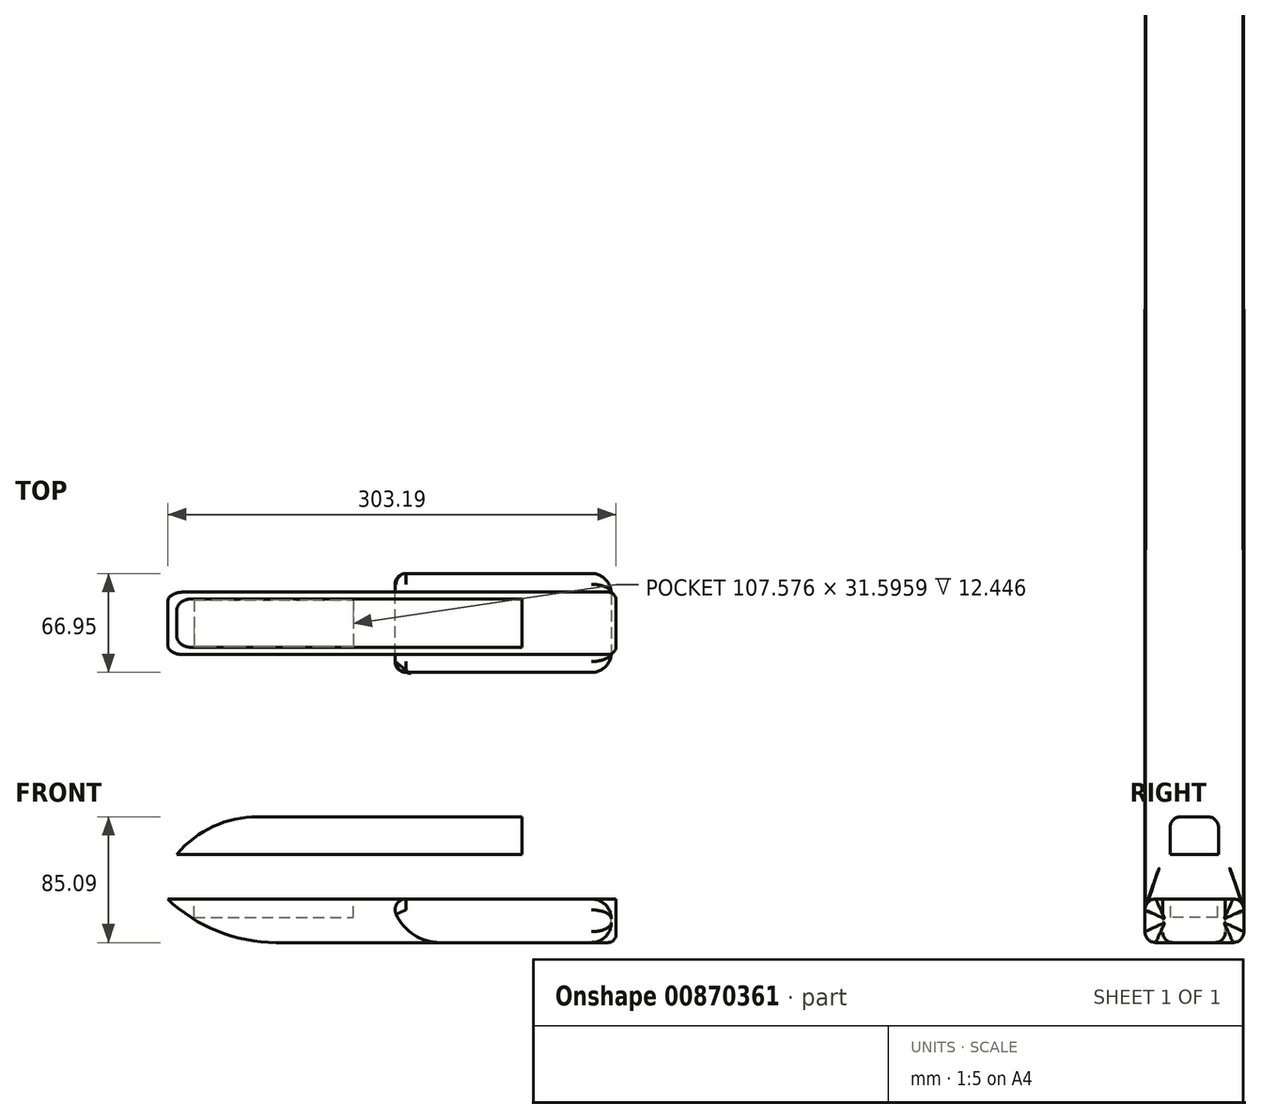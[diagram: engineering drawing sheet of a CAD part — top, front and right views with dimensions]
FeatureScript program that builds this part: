
annotation { "Feature Type Name" : "Feature", "Feature Type Description" : "" }
export const myFeature = defineFeature(function(context is Context, id is Id, definition is map)
    precondition{}
    {
        {
            var Q0;
            Q0=qCreatedBy(makeId("Top.planeOp"),FACE);
            var sketch = newSketch(context, id + "F0", { "sketchPlane" : qUnion([Q0])});
            skLineSegment(sketch, "E0.bottom", {"start": v(-65.35, -62.71) * mm, "end": v(74.53, -62.71) * mm});
            skLineSegment(sketch, "E0.top", {"start": v(-65.35, -29.97) * mm, "end": v(74.53, -29.97) * mm});
            skLineSegment(sketch, "E0.left", {"start": v(-65.35, -62.71) * mm, "end": v(-65.35, -29.97) * mm});
            skLineSegment(sketch, "E0.right", {"start": v(74.53, -62.71) * mm, "end": v(74.53, -29.97) * mm});
            skSolve(sketch);
        }
        {
            var Q0;
            Q0 = qSketchRegion(id + "F0", true);
            var Q1;
            Q1=makeQuery(id+"F0.imprint","IMPRINT",FACE,{"disambiguationData":[TD([[makeQuery(id+"F0.imprint","IMPRINT",EDGE,{"derivedFrom":sQuery(id+"F0.wireOp",EDGE,"E0.bottom")}),1.0]])]});
            extrude(context, id + "F1", {"entities" : qUnion([Q0, Q1]), "depth" : 25.4 * mm, "offsetDistance" : 25.4 * mm});
        }
        {
            var Q0;
            Q0=makeQuery(id+"F1.opExtrude","CAP_EDGE",EDGE,{"disambiguationData":[OSD([sQuery(id+"F0.wireOp",EDGE,"E0.left")])],"isStart":false});
            fillet(context, id + "F2", {"entities" : qUnion([Q0]), "radius" : 71.75 * mm, "tangentPropagation" : true, "allowEdgeOverflow" : false});
        }
        {
            var Q0;
            Q0=makeQuery(id+"F1.opExtrude","CAP_EDGE",EDGE,{"disambiguationData":[OSD([sQuery(id+"F0.wireOp",EDGE,"E0.bottom")])],"isStart":false});
            var Q1;
            Q1=makeQuery(id+"F1.opExtrude","CAP_EDGE",EDGE,{"disambiguationData":[OSD([sQuery(id+"F0.wireOp",EDGE,"E0.top")])],"isStart":false});
            fillet(context, id + "F3", {"entities" : qUnion([Q0, Q1]), "radius" : 7.36 * mm, "tangentPropagation" : true, "allowEdgeOverflow" : false});
        }
        {
            var Q0;
            Q0=makeQuery(id+"F1.opExtrude","SWEPT_FACE",FACE,{"disambiguationData":[OSD([sQuery(id+"F0.wireOp",EDGE,"E0.right")])]});
            extrude(context, id + "F4", {"entities" : qUnion([Q0]), "operationType" : NewBodyOperationType.ADD, "depth" : 93.22 * mm, "offsetDistance" : 25.4 * mm});
        }
        {
            var Q0;
            Q0=qCreatedBy(makeId("Top.planeOp"),FACE);
            cPlane(context, id + "F5", {"entities" : qUnion([Q0]), "cplaneType" : CPlaneType.OFFSET, "offset" : 30.23 * mm, "oppositeDirection" : true, "width" : 152.4 * mm, "height" : 152.4 * mm});
        }
        {
            var Q0;
            Q0=qCreatedBy(id+"F5.planeOp",FACE);
            var sketch = newSketch(context, id + "F6", { "sketchPlane" : qUnion([Q0])});
            skLineSegment(sketch, "E1.bottom", {"start": v(80.05, -12.74) * mm, "end": v(228.25, -12.74) * mm});
            skLineSegment(sketch, "E1.top", {"start": v(80.05, -79.7) * mm, "end": v(228.25, -79.7) * mm});
            skLineSegment(sketch, "E1.left", {"start": v(80.05, -12.74) * mm, "end": v(80.05, -79.7) * mm});
            skLineSegment(sketch, "E1.right", {"start": v(228.25, -12.74) * mm, "end": v(228.25, -79.7) * mm});
            skPoint(sketch, "E1.middle", {"position": v(154.15, -46.22) * mm});
            skSolve(sketch);
        }
        {
            var Q0;
            Q0=qCreatedBy(id+"F5.planeOp",FACE);
            var sketch = newSketch(context, id + "F7", { "sketchPlane" : qUnion([Q0])});
            skLineSegment(sketch, "E2.bottom", {"start": v(-71.65, -25.4) * mm, "end": v(231.54, -25.4) * mm});
            skLineSegment(sketch, "E2.top", {"start": v(-71.65, -67.57) * mm, "end": v(231.54, -67.57) * mm});
            skLineSegment(sketch, "E2.left", {"start": v(-71.65, -25.4) * mm, "end": v(-71.65, -67.57) * mm});
            skLineSegment(sketch, "E2.right", {"start": v(231.54, -25.4) * mm, "end": v(231.54, -67.57) * mm});
            skPoint(sketch, "E2.middle", {"position": v(79.94, -46.48) * mm});
            skSolve(sketch);
        }
        {
            var Q0;
            Q0=makeQuery(id+"F6.imprint","IMPRINT",FACE,{"disambiguationData":[TD([[makeQuery(id+"F6.imprint","IMPRINT",EDGE,{"derivedFrom":sQuery(id+"F6.wireOp",EDGE,"E1.bottom")}),-1.0]])]});
            var Q1;
            Q1=makeQuery(id+"F7.imprint","IMPRINT",FACE,{"disambiguationData":[TD([[makeQuery(id+"F7.imprint","IMPRINT",EDGE,{"derivedFrom":sQuery(id+"F7.wireOp",EDGE,"E2.bottom")}),-1.0]])]});
            extrude(context, id + "F8", {"entities" : qUnion([Q0, Q1]), "oppositeDirection" : true, "depth" : 29.46 * mm, "offsetDistance" : 25.4 * mm});
        }
        {
            var Q0;
            Q0=makeQuery(id+"F8.opExtrude","CAP_EDGE",EDGE,{"disambiguationData":[OSD([sQuery(id+"F7.wireOp",EDGE,"E2.left")])],"isStart":false});
            fillet(context, id + "F9", {"entities" : qUnion([Q0]), "radius" : 106.1 * mm, "tangentPropagation" : true, "allowEdgeOverflow" : false});
        }
        {
            var Q0;
            Q0=makeQuery(id+"F8.opExtrude","CAP_EDGE",EDGE,{"disambiguationData":[OSD([sQuery(id+"F7.wireOp",EDGE,"E2.top")])],"isStart":false});
            var Q1;
            Q1=makeQuery(id+"F8.opExtrude","CAP_EDGE",EDGE,{"disambiguationData":[OSD([sQuery(id+"F7.wireOp",EDGE,"E2.bottom")])],"isStart":false});
            fillet(context, id + "F10", {"entities" : qUnion([Q0, Q1]), "radius" : 6.75 * mm, "tangentPropagation" : true, "allowEdgeOverflow" : false});
        }
        {
            var Q0;
            Q0=makeQuery(id+"F8.opExtrude","CAP_EDGE",EDGE,{"disambiguationData":[OSD([sQuery(id+"F6.wireOp",EDGE,"E1.left")])],"isStart":false});
            fillet(context, id + "F11", {"entities" : qUnion([Q0]), "radius" : 32.5 * mm, "tangentPropagation" : true, "allowEdgeOverflow" : false});
        }
        {
            var Q0;
            {var subQ0=sQuery(id+"F6.wireOp",EDGE,"E1.left");Q0=makeQuery(id+"F11.opFillet","BLEND_EDGE",EDGE,{"blendedFrom":[makeQuery(id+"F8.opExtrude","CAP_EDGE",EDGE,{"disambiguationData":[OSD([subQ0])],"isStart":false}),makeQuery(id+"F8.opExtrude","CAP_FACE",FACE,{"disambiguationData":[OSD([sQuery(id+"F6.wireOp",EDGE,"E1.bottom"),sQuery(id+"F6.wireOp",EDGE,"E1.top"),subQ0,sQuery(id+"F6.wireOp",EDGE,"E1.right")])],"isStart":true})],"blendedInto":[makeQuery(id+"F8.opExtrude","CAP_FACE",FACE,{"disambiguationData":[OSD([sQuery(id+"F6.wireOp",EDGE,"E1.bottom"),sQuery(id+"F6.wireOp",EDGE,"E1.top"),subQ0,sQuery(id+"F6.wireOp",EDGE,"E1.right")])],"isStart":true})]});}
            fillet(context, id + "F12", {"entities" : qUnion([Q0]), "radius" : 7.33 * mm, "tangentPropagation" : true, "allowEdgeOverflow" : false});
        }
        {
            var Q0;
            Q0=makeQuery(id+"F8.opExtrude","CAP_EDGE",EDGE,{"disambiguationData":[OSD([sQuery(id+"F6.wireOp",EDGE,"E1.top")])],"isStart":false});
            var Q1;
            Q1=makeQuery(id+"F8.opExtrude","CAP_EDGE",EDGE,{"disambiguationData":[OSD([sQuery(id+"F6.wireOp",EDGE,"E1.bottom")])],"isStart":false});
            fillet(context, id + "F13", {"entities" : qUnion([Q0, Q1]), "radius" : 7.36 * mm, "tangentPropagation" : true, "allowEdgeOverflow" : false});
        }
        {
            var Q0;
            Q0=makeQuery(id+"F8.opExtrude","CAP_EDGE",EDGE,{"disambiguationData":[OSD([sQuery(id+"F7.wireOp",EDGE,"E2.right")])],"isStart":false});
            fillet(context, id + "F14", {"entities" : qUnion([Q0]), "radius" : 5.52 * mm, "tangentPropagation" : true, "allowEdgeOverflow" : false});
        }
        {
            var Q0;
            Q0=makeQuery(id+"F8.opExtrude","CAP_EDGE",EDGE,{"disambiguationData":[OSD([sQuery(id+"F6.wireOp",EDGE,"E1.right")])],"isStart":false});
            fillet(context, id + "F15", {"entities" : qUnion([Q0]), "radius" : 13.5 * mm, "tangentPropagation" : true, "allowEdgeOverflow" : false});
        }
        {
            var Q0;
            Q0=qCreatedBy(id+"F5.planeOp",FACE);
            var sketch = newSketch(context, id + "F16", { "sketchPlane" : qUnion([Q0])});
            skLineSegment(sketch, "E3.bottom", {"start": v(-53.79, -30.66) * mm, "end": v(53.79, -30.66) * mm});
            skLineSegment(sketch, "E3.top", {"start": v(-53.79, -62.25) * mm, "end": v(53.79, -62.25) * mm});
            skLineSegment(sketch, "E3.left", {"start": v(-53.79, -30.66) * mm, "end": v(-53.79, -62.25) * mm});
            skLineSegment(sketch, "E3.right", {"start": v(53.79, -30.66) * mm, "end": v(53.79, -62.25) * mm});
            skPoint(sketch, "E3.middle", {"position": v(0, -46.45) * mm});
            skSolve(sketch);
        }
        {
            var Q0;
            Q0=makeQuery(id+"F16.imprint","IMPRINT",FACE,{"disambiguationData":[TD([[makeQuery(id+"F16.imprint","IMPRINT",EDGE,{"derivedFrom":sQuery(id+"F16.wireOp",EDGE,"E3.bottom")}),-1.0]])]});
            extrude(context, id + "F17", {"entities" : qUnion([Q0]), "operationType" : NewBodyOperationType.REMOVE, "oppositeDirection" : true, "depth" : 12.45 * mm, "offsetDistance" : 25.4 * mm});
        }
    });
